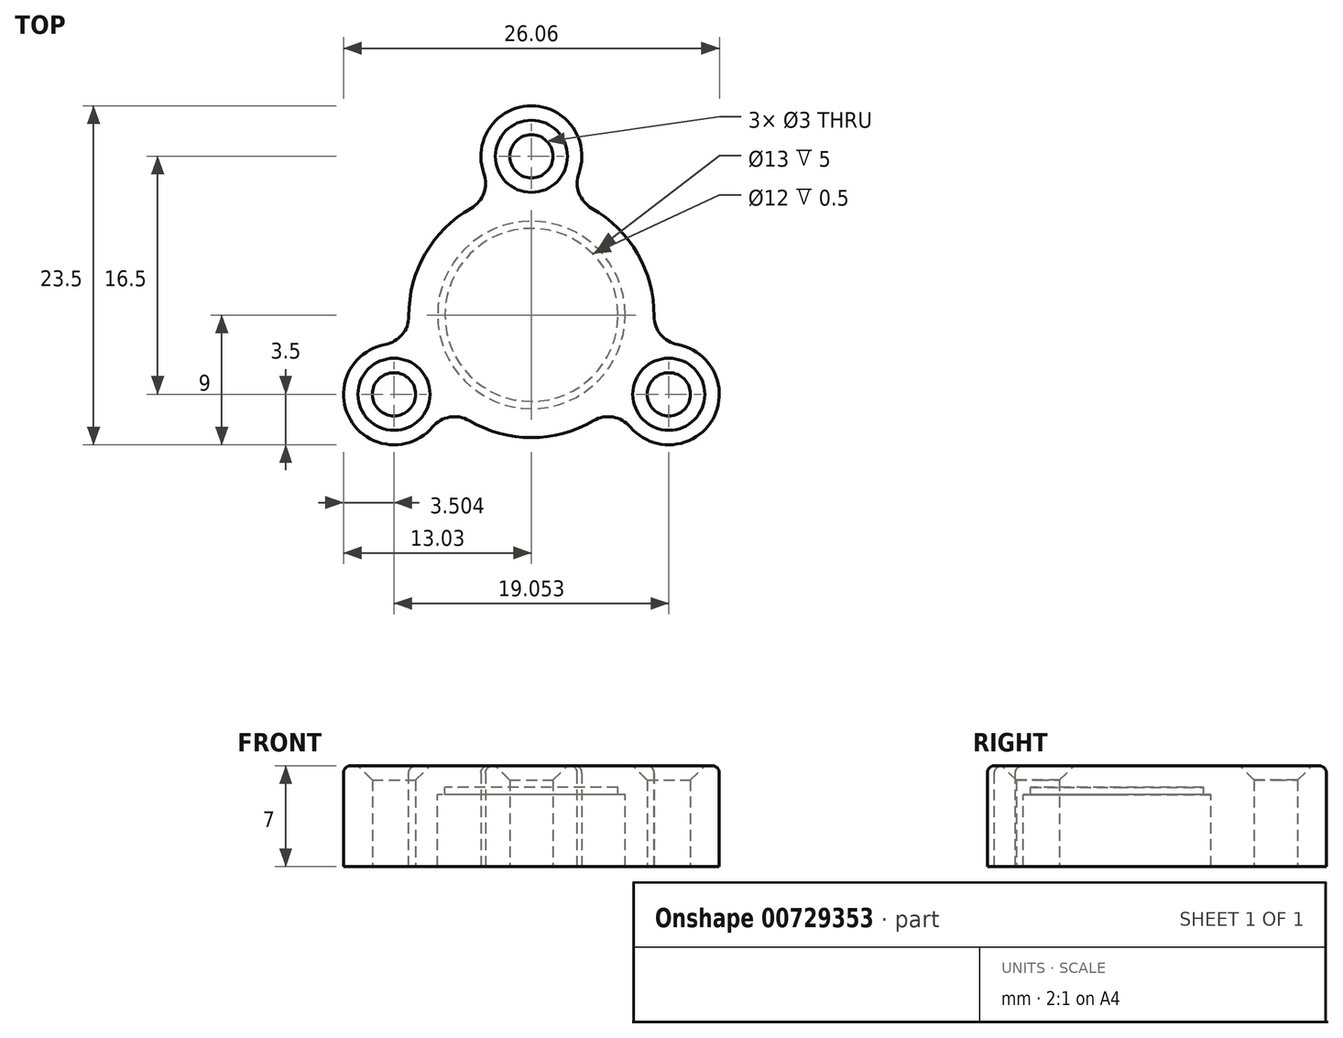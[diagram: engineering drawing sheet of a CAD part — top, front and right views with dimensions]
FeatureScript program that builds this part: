
annotation { "Feature Type Name" : "Feature", "Feature Type Description" : "" }
export const myFeature = defineFeature(function(context is Context, id is Id, definition is map)
    precondition{}
    {
        {
            var Q0;
            Q0=qCreatedBy(makeId("Right.planeOp"),FACE);
            var sketch = newSketch(context, id + "F0", { "sketchPlane" : qUnion([Q0])});
            skLineSegment(sketch, "E0", {"start": v(-8.5, 0) * mm, "end": v(-8.5, 7) * mm});
            skLineSegment(sketch, "E1", {"start": v(-8.5, 7) * mm, "end": v(0, 7) * mm});
            skLineSegment(sketch, "E2", {"start": v(0, 7) * mm, "end": v(0, 5.5) * mm});
            skLineSegment(sketch, "E3", {"start": v(-6, 5) * mm, "end": v(-6.5, 5) * mm});
            skLineSegment(sketch, "E4", {"start": v(-6.5, 5) * mm, "end": v(-6.5, 0) * mm});
            skLineSegment(sketch, "E5", {"start": v(-6.5, 0) * mm, "end": v(-8.5, 0) * mm});
            skLineSegment(sketch, "E6.top", {"start": v(-6, 5.5) * mm, "end": v(0, 5.5) * mm});
            skLineSegment(sketch, "E6.left", {"start": v(-6, 5) * mm, "end": v(-6, 5.5) * mm});
            skSolve(sketch);
        }
        {
            var Q0;
            Q0=makeQuery(id+"F0.imprint","IMPRINT",FACE,{"disambiguationData":[TD([[makeQuery(id+"F0.imprint","IMPRINT",EDGE,{"derivedFrom":sQuery(id+"F0.wireOp",EDGE,"E0")}),-1.0]])]});
            var Q1;
            Q1=sQuery(id+"F0.wireOp",EDGE,"E2");
            revolve(context, id + "F1", {"surfaceOperationType" : NewSurfaceOperationType.NEW, "entities" : qUnion([Q0]), "axis" : qUnion([Q1]), "revolveType" : RevolveType.FULL});
        }
        {
            var Q0;
            Q0=qCreatedBy(makeId("Top.planeOp"),FACE);
            var sketch = newSketch(context, id + "F2", { "sketchPlane" : qUnion([Q0])});
            skLineSegment(sketch, "E7", {"start": v(0, 11) * mm, "end": v(0, -13.89) * mm, "construction": true});
            skCircle(sketch, "E8", {"center": v(0, 11) * mm, "radius": 3.5 * mm});
            skCircle(sketch, "E9", {"center": v(0, 11) * mm, "radius": 1.5 * mm});
            skPoint(sketch, "E10", {"position": v(0, 0) * mm});
            skCircle(sketch, "E11.1.0", {"center": v(-9.53, -5.5) * mm, "radius": 3.5 * mm});
            skCircle(sketch, "E11.1.1", {"center": v(-9.53, -5.5) * mm, "radius": 1.5 * mm});
            skCircle(sketch, "E11.2.0", {"center": v(9.53, -5.5) * mm, "radius": 3.5 * mm});
            skCircle(sketch, "E11.2.1", {"center": v(9.53, -5.5) * mm, "radius": 1.5 * mm});
            skSolve(sketch);
        }
        {
            var Q0;
            Q0=makeQuery(id+"F2.imprint","IMPRINT",FACE,{"disambiguationData":[TD([[makeQuery(id+"F2.imprint","IMPRINT",EDGE,{"derivedFrom":sQuery(id+"F2.wireOp",EDGE,"E8")}),1.0]])]});
            var Q1;
            Q1=makeQuery(id+"F2.imprint","IMPRINT",FACE,{"disambiguationData":[TD([[makeQuery(id+"F2.imprint","IMPRINT",EDGE,{"derivedFrom":sQuery(id+"F2.wireOp",EDGE,"E11.1.0")}),1.0]])]});
            var Q2;
            Q2=makeQuery(id+"F2.imprint","IMPRINT",FACE,{"disambiguationData":[TD([[makeQuery(id+"F2.imprint","IMPRINT",EDGE,{"derivedFrom":sQuery(id+"F2.wireOp",EDGE,"E11.2.0")}),1.0]])]});
            extrude(context, id + "F3", {"entities" : qUnion([Q0, Q1, Q2]), "operationType" : NewBodyOperationType.ADD, "depth" : 7 * mm, "offsetDistance" : 25 * mm});
        }
        {
            var Q0;
            Q0=makeQuery(id+"F3.opExtrude","CAP_EDGE",EDGE,{"disambiguationData":[OSD([sQuery(id+"F2.wireOp",EDGE,"E9")])],"isStart":false});
            var Q1;
            Q1=makeQuery(id+"F3.opExtrude","CAP_EDGE",EDGE,{"disambiguationData":[OSD([sQuery(id+"F2.wireOp",EDGE,"E11.1.1")])],"isStart":false});
            var Q2;
            Q2=makeQuery(id+"F3.opExtrude","CAP_EDGE",EDGE,{"disambiguationData":[OSD([sQuery(id+"F2.wireOp",EDGE,"E11.2.1")])],"isStart":false});
            chamfer(context, id + "F4", {"entities" : qUnion([Q0, Q1, Q2]), "width" : 1 * mm, "tangentPropagation" : true});
        }
        {
            var Q0;
            Q0=makeQuery(id+"F3.boolean.opBoolean","INTERSECT",EDGE,{"disambiguationData":[OD(0.0)],"derivedFrom":[makeQuery(id+"F1.opRevolve","SWEPT_FACE",FACE,{"disambiguationData":[OSD([sQuery(id+"F0.wireOp",EDGE,"E0")])]}),makeQuery(id+"F3.opExtrude","SWEPT_FACE",FACE,{"disambiguationData":[OSD([sQuery(id+"F2.wireOp",EDGE,"E8")])]})]});
            var Q1;
            Q1=makeQuery(id+"F3.boolean.opBoolean","INTERSECT",EDGE,{"disambiguationData":[OD(0.0)],"derivedFrom":[makeQuery(id+"F1.opRevolve","SWEPT_FACE",FACE,{"disambiguationData":[OSD([sQuery(id+"F0.wireOp",EDGE,"E0")])]}),makeQuery(id+"F3.opExtrude","SWEPT_FACE",FACE,{"disambiguationData":[OSD([sQuery(id+"F2.wireOp",EDGE,"E11.1.0")])]})]});
            var Q2;
            Q2=makeQuery(id+"F3.boolean.opBoolean","INTERSECT",EDGE,{"disambiguationData":[OD(1.0)],"derivedFrom":[makeQuery(id+"F1.opRevolve","SWEPT_FACE",FACE,{"disambiguationData":[OSD([sQuery(id+"F0.wireOp",EDGE,"E0")])]}),makeQuery(id+"F3.opExtrude","SWEPT_FACE",FACE,{"disambiguationData":[OSD([sQuery(id+"F2.wireOp",EDGE,"E11.1.0")])]})]});
            var Q3;
            Q3=makeQuery(id+"F3.boolean.opBoolean","INTERSECT",EDGE,{"disambiguationData":[OD(1.0)],"derivedFrom":[makeQuery(id+"F1.opRevolve","SWEPT_FACE",FACE,{"disambiguationData":[OSD([sQuery(id+"F0.wireOp",EDGE,"E0")])]}),makeQuery(id+"F3.opExtrude","SWEPT_FACE",FACE,{"disambiguationData":[OSD([sQuery(id+"F2.wireOp",EDGE,"E11.2.0")])]})]});
            var Q4;
            Q4=makeQuery(id+"F3.boolean.opBoolean","INTERSECT",EDGE,{"disambiguationData":[OD(0.0)],"derivedFrom":[makeQuery(id+"F1.opRevolve","SWEPT_FACE",FACE,{"disambiguationData":[OSD([sQuery(id+"F0.wireOp",EDGE,"E0")])]}),makeQuery(id+"F3.opExtrude","SWEPT_FACE",FACE,{"disambiguationData":[OSD([sQuery(id+"F2.wireOp",EDGE,"E11.2.0")])]})]});
            var Q5;
            Q5=makeQuery(id+"F3.boolean.opBoolean","INTERSECT",EDGE,{"disambiguationData":[OD(1.0)],"derivedFrom":[makeQuery(id+"F1.opRevolve","SWEPT_FACE",FACE,{"disambiguationData":[OSD([sQuery(id+"F0.wireOp",EDGE,"E0")])]}),makeQuery(id+"F3.opExtrude","SWEPT_FACE",FACE,{"disambiguationData":[OSD([sQuery(id+"F2.wireOp",EDGE,"E8")])]})]});
            fillet(context, id + "F5", {"entities" : qUnion([Q0, Q1, Q2, Q3, Q4, Q5]), "radius" : 2 * mm, "tangentPropagation" : true, "allowEdgeOverflow" : false});
        }
        {
            var Q0;
            {var subQ0=sQuery(id+"F2.wireOp",EDGE,"E11.1.0");var subQ1=sQuery(id+"F0.wireOp",EDGE,"E1");var subQ2=sQuery(id+"F0.wireOp",EDGE,"E0");var subQ3=sQuery(id+"F2.wireOp",EDGE,"E11.2.0");Q0=makeQuery(id+"F3.boolean.opBoolean","SPLIT",EDGE,{"disambiguationData":[TD([makeQuery(id+"F1.opRevolve","SWEPT_FACE",FACE,{"disambiguationData":[OSD([subQ2])]}),makeQuery(id+"F1.opRevolve","SWEPT_FACE",FACE,{"disambiguationData":[OSD([subQ1])]}),makeQuery(id+"F3.opExtrude","CAP_FACE",FACE,{"disambiguationData":[OSD([sQuery(id+"F2.wireOp",EDGE,"E8"),sQuery(id+"F2.wireOp",EDGE,"E9")])],"isStart":false}),makeQuery(id+"F3.opExtrude","SWEPT_FACE",FACE,{"disambiguationData":[OSD([subQ0])]}),makeQuery(id+"F3.opExtrude","CAP_FACE",FACE,{"disambiguationData":[OSD([subQ0,sQuery(id+"F2.wireOp",EDGE,"E11.1.1")])],"isStart":false}),makeQuery(id+"F3.opExtrude","SWEPT_FACE",FACE,{"disambiguationData":[OSD([subQ3])]}),makeQuery(id+"F3.opExtrude","CAP_FACE",FACE,{"disambiguationData":[OSD([subQ3,sQuery(id+"F2.wireOp",EDGE,"E11.2.1")])],"isStart":false})])],"derivedFrom":makeQuery(id+"F1.opRevolve","SWEPT_EDGE",EDGE,{"disambiguationData":[OSD([subQ2,subQ1])]})});}
            var Q1;
            {var subQ0=sQuery(id+"F2.wireOp",EDGE,"E11.1.0");Q1=makeQuery(id+"F5.opFillet","BLEND_EDGE",EDGE,{"blendedFrom":[makeQuery(id+"F3.boolean.opBoolean","INTERSECT",EDGE,{"disambiguationData":[OD(1.0)],"derivedFrom":[makeQuery(id+"F1.opRevolve","SWEPT_FACE",FACE,{"disambiguationData":[OSD([sQuery(id+"F0.wireOp",EDGE,"E0")])]}),makeQuery(id+"F3.opExtrude","SWEPT_FACE",FACE,{"disambiguationData":[OSD([subQ0])]})]}),makeQuery(id+"F3.boolean.opBoolean","MERGE",FACE,{"derivedFrom":[makeQuery(id+"F1.opRevolve","SWEPT_FACE",FACE,{"disambiguationData":[OSD([sQuery(id+"F0.wireOp",EDGE,"E1")])]}),makeQuery(id+"F3.opExtrude","CAP_FACE",FACE,{"disambiguationData":[OSD([sQuery(id+"F2.wireOp",EDGE,"E8"),sQuery(id+"F2.wireOp",EDGE,"E9")])],"isStart":false}),makeQuery(id+"F3.opExtrude","CAP_FACE",FACE,{"disambiguationData":[OSD([subQ0,sQuery(id+"F2.wireOp",EDGE,"E11.1.1")])],"isStart":false}),makeQuery(id+"F3.opExtrude","CAP_FACE",FACE,{"disambiguationData":[OSD([sQuery(id+"F2.wireOp",EDGE,"E11.2.0"),sQuery(id+"F2.wireOp",EDGE,"E11.2.1")])],"isStart":false})]})],"blendedInto":[makeQuery(id+"F3.boolean.opBoolean","MERGE",FACE,{"derivedFrom":[makeQuery(id+"F1.opRevolve","SWEPT_FACE",FACE,{"disambiguationData":[OSD([sQuery(id+"F0.wireOp",EDGE,"E1")])]}),makeQuery(id+"F3.opExtrude","CAP_FACE",FACE,{"disambiguationData":[OSD([sQuery(id+"F2.wireOp",EDGE,"E8"),sQuery(id+"F2.wireOp",EDGE,"E9")])],"isStart":false}),makeQuery(id+"F3.opExtrude","CAP_FACE",FACE,{"disambiguationData":[OSD([subQ0,sQuery(id+"F2.wireOp",EDGE,"E11.1.1")])],"isStart":false}),makeQuery(id+"F3.opExtrude","CAP_FACE",FACE,{"disambiguationData":[OSD([sQuery(id+"F2.wireOp",EDGE,"E11.2.0"),sQuery(id+"F2.wireOp",EDGE,"E11.2.1")])],"isStart":false})]})]});}
            var Q2;
            Q2=makeQuery(id+"F3.opExtrude","CAP_EDGE",EDGE,{"disambiguationData":[OSD([sQuery(id+"F2.wireOp",EDGE,"E11.1.0")])],"isStart":false});
            var Q3;
            {var subQ0=sQuery(id+"F2.wireOp",EDGE,"E11.1.0");Q3=makeQuery(id+"F5.opFillet","BLEND_EDGE",EDGE,{"blendedFrom":[makeQuery(id+"F3.boolean.opBoolean","INTERSECT",EDGE,{"disambiguationData":[OD(0.0)],"derivedFrom":[makeQuery(id+"F1.opRevolve","SWEPT_FACE",FACE,{"disambiguationData":[OSD([sQuery(id+"F0.wireOp",EDGE,"E0")])]}),makeQuery(id+"F3.opExtrude","SWEPT_FACE",FACE,{"disambiguationData":[OSD([subQ0])]})]}),makeQuery(id+"F3.boolean.opBoolean","MERGE",FACE,{"derivedFrom":[makeQuery(id+"F1.opRevolve","SWEPT_FACE",FACE,{"disambiguationData":[OSD([sQuery(id+"F0.wireOp",EDGE,"E1")])]}),makeQuery(id+"F3.opExtrude","CAP_FACE",FACE,{"disambiguationData":[OSD([sQuery(id+"F2.wireOp",EDGE,"E8"),sQuery(id+"F2.wireOp",EDGE,"E9")])],"isStart":false}),makeQuery(id+"F3.opExtrude","CAP_FACE",FACE,{"disambiguationData":[OSD([subQ0,sQuery(id+"F2.wireOp",EDGE,"E11.1.1")])],"isStart":false}),makeQuery(id+"F3.opExtrude","CAP_FACE",FACE,{"disambiguationData":[OSD([sQuery(id+"F2.wireOp",EDGE,"E11.2.0"),sQuery(id+"F2.wireOp",EDGE,"E11.2.1")])],"isStart":false})]})],"blendedInto":[makeQuery(id+"F3.boolean.opBoolean","MERGE",FACE,{"derivedFrom":[makeQuery(id+"F1.opRevolve","SWEPT_FACE",FACE,{"disambiguationData":[OSD([sQuery(id+"F0.wireOp",EDGE,"E1")])]}),makeQuery(id+"F3.opExtrude","CAP_FACE",FACE,{"disambiguationData":[OSD([sQuery(id+"F2.wireOp",EDGE,"E8"),sQuery(id+"F2.wireOp",EDGE,"E9")])],"isStart":false}),makeQuery(id+"F3.opExtrude","CAP_FACE",FACE,{"disambiguationData":[OSD([subQ0,sQuery(id+"F2.wireOp",EDGE,"E11.1.1")])],"isStart":false}),makeQuery(id+"F3.opExtrude","CAP_FACE",FACE,{"disambiguationData":[OSD([sQuery(id+"F2.wireOp",EDGE,"E11.2.0"),sQuery(id+"F2.wireOp",EDGE,"E11.2.1")])],"isStart":false})]})]});}
            var Q4;
            {var subQ0=sQuery(id+"F2.wireOp",EDGE,"E8");var subQ1=sQuery(id+"F0.wireOp",EDGE,"E1");var subQ2=sQuery(id+"F0.wireOp",EDGE,"E0");var subQ3=sQuery(id+"F2.wireOp",EDGE,"E11.1.0");Q4=makeQuery(id+"F3.boolean.opBoolean","SPLIT",EDGE,{"disambiguationData":[TD([makeQuery(id+"F1.opRevolve","SWEPT_FACE",FACE,{"disambiguationData":[OSD([subQ2])]}),makeQuery(id+"F1.opRevolve","SWEPT_FACE",FACE,{"disambiguationData":[OSD([subQ1])]}),makeQuery(id+"F3.opExtrude","SWEPT_FACE",FACE,{"disambiguationData":[OSD([subQ0])]}),makeQuery(id+"F3.opExtrude","CAP_FACE",FACE,{"disambiguationData":[OSD([subQ0,sQuery(id+"F2.wireOp",EDGE,"E9")])],"isStart":false}),makeQuery(id+"F3.opExtrude","SWEPT_FACE",FACE,{"disambiguationData":[OSD([subQ3])]}),makeQuery(id+"F3.opExtrude","CAP_FACE",FACE,{"disambiguationData":[OSD([subQ3,sQuery(id+"F2.wireOp",EDGE,"E11.1.1")])],"isStart":false}),makeQuery(id+"F3.opExtrude","CAP_FACE",FACE,{"disambiguationData":[OSD([sQuery(id+"F2.wireOp",EDGE,"E11.2.0"),sQuery(id+"F2.wireOp",EDGE,"E11.2.1")])],"isStart":false})])],"derivedFrom":makeQuery(id+"F1.opRevolve","SWEPT_EDGE",EDGE,{"disambiguationData":[OSD([subQ2,subQ1])]})});}
            var Q5;
            {var subQ0=sQuery(id+"F2.wireOp",EDGE,"E8");Q5=makeQuery(id+"F5.opFillet","BLEND_EDGE",EDGE,{"blendedFrom":[makeQuery(id+"F3.boolean.opBoolean","INTERSECT",EDGE,{"disambiguationData":[OD(0.0)],"derivedFrom":[makeQuery(id+"F1.opRevolve","SWEPT_FACE",FACE,{"disambiguationData":[OSD([sQuery(id+"F0.wireOp",EDGE,"E0")])]}),makeQuery(id+"F3.opExtrude","SWEPT_FACE",FACE,{"disambiguationData":[OSD([subQ0])]})]}),makeQuery(id+"F3.boolean.opBoolean","MERGE",FACE,{"derivedFrom":[makeQuery(id+"F1.opRevolve","SWEPT_FACE",FACE,{"disambiguationData":[OSD([sQuery(id+"F0.wireOp",EDGE,"E1")])]}),makeQuery(id+"F3.opExtrude","CAP_FACE",FACE,{"disambiguationData":[OSD([subQ0,sQuery(id+"F2.wireOp",EDGE,"E9")])],"isStart":false}),makeQuery(id+"F3.opExtrude","CAP_FACE",FACE,{"disambiguationData":[OSD([sQuery(id+"F2.wireOp",EDGE,"E11.1.0"),sQuery(id+"F2.wireOp",EDGE,"E11.1.1")])],"isStart":false}),makeQuery(id+"F3.opExtrude","CAP_FACE",FACE,{"disambiguationData":[OSD([sQuery(id+"F2.wireOp",EDGE,"E11.2.0"),sQuery(id+"F2.wireOp",EDGE,"E11.2.1")])],"isStart":false})]})],"blendedInto":[makeQuery(id+"F3.boolean.opBoolean","MERGE",FACE,{"derivedFrom":[makeQuery(id+"F1.opRevolve","SWEPT_FACE",FACE,{"disambiguationData":[OSD([sQuery(id+"F0.wireOp",EDGE,"E1")])]}),makeQuery(id+"F3.opExtrude","CAP_FACE",FACE,{"disambiguationData":[OSD([subQ0,sQuery(id+"F2.wireOp",EDGE,"E9")])],"isStart":false}),makeQuery(id+"F3.opExtrude","CAP_FACE",FACE,{"disambiguationData":[OSD([sQuery(id+"F2.wireOp",EDGE,"E11.1.0"),sQuery(id+"F2.wireOp",EDGE,"E11.1.1")])],"isStart":false}),makeQuery(id+"F3.opExtrude","CAP_FACE",FACE,{"disambiguationData":[OSD([sQuery(id+"F2.wireOp",EDGE,"E11.2.0"),sQuery(id+"F2.wireOp",EDGE,"E11.2.1")])],"isStart":false})]})]});}
            var Q6;
            Q6=makeQuery(id+"F3.opExtrude","CAP_EDGE",EDGE,{"disambiguationData":[OSD([sQuery(id+"F2.wireOp",EDGE,"E8")])],"isStart":false});
            var Q7;
            {var subQ0=sQuery(id+"F2.wireOp",EDGE,"E8");var subQ1=sQuery(id+"F0.wireOp",EDGE,"E1");var subQ2=sQuery(id+"F0.wireOp",EDGE,"E0");var subQ3=sQuery(id+"F2.wireOp",EDGE,"E11.2.0");Q7=makeQuery(id+"F3.boolean.opBoolean","SPLIT",EDGE,{"disambiguationData":[TD([makeQuery(id+"F1.opRevolve","SWEPT_FACE",FACE,{"disambiguationData":[OSD([subQ2])]}),makeQuery(id+"F1.opRevolve","SWEPT_FACE",FACE,{"disambiguationData":[OSD([subQ1])]}),makeQuery(id+"F3.opExtrude","SWEPT_FACE",FACE,{"disambiguationData":[OSD([subQ0])]}),makeQuery(id+"F3.opExtrude","CAP_FACE",FACE,{"disambiguationData":[OSD([subQ0,sQuery(id+"F2.wireOp",EDGE,"E9")])],"isStart":false}),makeQuery(id+"F3.opExtrude","CAP_FACE",FACE,{"disambiguationData":[OSD([sQuery(id+"F2.wireOp",EDGE,"E11.1.0"),sQuery(id+"F2.wireOp",EDGE,"E11.1.1")])],"isStart":false}),makeQuery(id+"F3.opExtrude","SWEPT_FACE",FACE,{"disambiguationData":[OSD([subQ3])]}),makeQuery(id+"F3.opExtrude","CAP_FACE",FACE,{"disambiguationData":[OSD([subQ3,sQuery(id+"F2.wireOp",EDGE,"E11.2.1")])],"isStart":false})])],"derivedFrom":makeQuery(id+"F1.opRevolve","SWEPT_EDGE",EDGE,{"disambiguationData":[OSD([subQ2,subQ1])]})});}
            var Q8;
            {var subQ0=sQuery(id+"F2.wireOp",EDGE,"E8");Q8=makeQuery(id+"F5.opFillet","BLEND_EDGE",EDGE,{"blendedFrom":[makeQuery(id+"F3.boolean.opBoolean","INTERSECT",EDGE,{"disambiguationData":[OD(1.0)],"derivedFrom":[makeQuery(id+"F1.opRevolve","SWEPT_FACE",FACE,{"disambiguationData":[OSD([sQuery(id+"F0.wireOp",EDGE,"E0")])]}),makeQuery(id+"F3.opExtrude","SWEPT_FACE",FACE,{"disambiguationData":[OSD([subQ0])]})]}),makeQuery(id+"F3.boolean.opBoolean","MERGE",FACE,{"derivedFrom":[makeQuery(id+"F1.opRevolve","SWEPT_FACE",FACE,{"disambiguationData":[OSD([sQuery(id+"F0.wireOp",EDGE,"E1")])]}),makeQuery(id+"F3.opExtrude","CAP_FACE",FACE,{"disambiguationData":[OSD([subQ0,sQuery(id+"F2.wireOp",EDGE,"E9")])],"isStart":false}),makeQuery(id+"F3.opExtrude","CAP_FACE",FACE,{"disambiguationData":[OSD([sQuery(id+"F2.wireOp",EDGE,"E11.1.0"),sQuery(id+"F2.wireOp",EDGE,"E11.1.1")])],"isStart":false}),makeQuery(id+"F3.opExtrude","CAP_FACE",FACE,{"disambiguationData":[OSD([sQuery(id+"F2.wireOp",EDGE,"E11.2.0"),sQuery(id+"F2.wireOp",EDGE,"E11.2.1")])],"isStart":false})]})],"blendedInto":[makeQuery(id+"F3.boolean.opBoolean","MERGE",FACE,{"derivedFrom":[makeQuery(id+"F1.opRevolve","SWEPT_FACE",FACE,{"disambiguationData":[OSD([sQuery(id+"F0.wireOp",EDGE,"E1")])]}),makeQuery(id+"F3.opExtrude","CAP_FACE",FACE,{"disambiguationData":[OSD([subQ0,sQuery(id+"F2.wireOp",EDGE,"E9")])],"isStart":false}),makeQuery(id+"F3.opExtrude","CAP_FACE",FACE,{"disambiguationData":[OSD([sQuery(id+"F2.wireOp",EDGE,"E11.1.0"),sQuery(id+"F2.wireOp",EDGE,"E11.1.1")])],"isStart":false}),makeQuery(id+"F3.opExtrude","CAP_FACE",FACE,{"disambiguationData":[OSD([sQuery(id+"F2.wireOp",EDGE,"E11.2.0"),sQuery(id+"F2.wireOp",EDGE,"E11.2.1")])],"isStart":false})]})]});}
            var Q9;
            {var subQ0=sQuery(id+"F2.wireOp",EDGE,"E11.2.0");Q9=makeQuery(id+"F5.opFillet","BLEND_EDGE",EDGE,{"blendedFrom":[makeQuery(id+"F3.boolean.opBoolean","INTERSECT",EDGE,{"disambiguationData":[OD(0.0)],"derivedFrom":[makeQuery(id+"F1.opRevolve","SWEPT_FACE",FACE,{"disambiguationData":[OSD([sQuery(id+"F0.wireOp",EDGE,"E0")])]}),makeQuery(id+"F3.opExtrude","SWEPT_FACE",FACE,{"disambiguationData":[OSD([subQ0])]})]}),makeQuery(id+"F3.boolean.opBoolean","MERGE",FACE,{"derivedFrom":[makeQuery(id+"F1.opRevolve","SWEPT_FACE",FACE,{"disambiguationData":[OSD([sQuery(id+"F0.wireOp",EDGE,"E1")])]}),makeQuery(id+"F3.opExtrude","CAP_FACE",FACE,{"disambiguationData":[OSD([sQuery(id+"F2.wireOp",EDGE,"E8"),sQuery(id+"F2.wireOp",EDGE,"E9")])],"isStart":false}),makeQuery(id+"F3.opExtrude","CAP_FACE",FACE,{"disambiguationData":[OSD([sQuery(id+"F2.wireOp",EDGE,"E11.1.0"),sQuery(id+"F2.wireOp",EDGE,"E11.1.1")])],"isStart":false}),makeQuery(id+"F3.opExtrude","CAP_FACE",FACE,{"disambiguationData":[OSD([subQ0,sQuery(id+"F2.wireOp",EDGE,"E11.2.1")])],"isStart":false})]})],"blendedInto":[makeQuery(id+"F3.boolean.opBoolean","MERGE",FACE,{"derivedFrom":[makeQuery(id+"F1.opRevolve","SWEPT_FACE",FACE,{"disambiguationData":[OSD([sQuery(id+"F0.wireOp",EDGE,"E1")])]}),makeQuery(id+"F3.opExtrude","CAP_FACE",FACE,{"disambiguationData":[OSD([sQuery(id+"F2.wireOp",EDGE,"E8"),sQuery(id+"F2.wireOp",EDGE,"E9")])],"isStart":false}),makeQuery(id+"F3.opExtrude","CAP_FACE",FACE,{"disambiguationData":[OSD([sQuery(id+"F2.wireOp",EDGE,"E11.1.0"),sQuery(id+"F2.wireOp",EDGE,"E11.1.1")])],"isStart":false}),makeQuery(id+"F3.opExtrude","CAP_FACE",FACE,{"disambiguationData":[OSD([subQ0,sQuery(id+"F2.wireOp",EDGE,"E11.2.1")])],"isStart":false})]})]});}
            var Q10;
            Q10=makeQuery(id+"F3.opExtrude","CAP_EDGE",EDGE,{"disambiguationData":[OSD([sQuery(id+"F2.wireOp",EDGE,"E11.2.0")])],"isStart":false});
            var Q11;
            {var subQ0=sQuery(id+"F2.wireOp",EDGE,"E11.2.0");Q11=makeQuery(id+"F5.opFillet","BLEND_EDGE",EDGE,{"blendedFrom":[makeQuery(id+"F3.boolean.opBoolean","INTERSECT",EDGE,{"disambiguationData":[OD(1.0)],"derivedFrom":[makeQuery(id+"F1.opRevolve","SWEPT_FACE",FACE,{"disambiguationData":[OSD([sQuery(id+"F0.wireOp",EDGE,"E0")])]}),makeQuery(id+"F3.opExtrude","SWEPT_FACE",FACE,{"disambiguationData":[OSD([subQ0])]})]}),makeQuery(id+"F3.boolean.opBoolean","MERGE",FACE,{"derivedFrom":[makeQuery(id+"F1.opRevolve","SWEPT_FACE",FACE,{"disambiguationData":[OSD([sQuery(id+"F0.wireOp",EDGE,"E1")])]}),makeQuery(id+"F3.opExtrude","CAP_FACE",FACE,{"disambiguationData":[OSD([sQuery(id+"F2.wireOp",EDGE,"E8"),sQuery(id+"F2.wireOp",EDGE,"E9")])],"isStart":false}),makeQuery(id+"F3.opExtrude","CAP_FACE",FACE,{"disambiguationData":[OSD([sQuery(id+"F2.wireOp",EDGE,"E11.1.0"),sQuery(id+"F2.wireOp",EDGE,"E11.1.1")])],"isStart":false}),makeQuery(id+"F3.opExtrude","CAP_FACE",FACE,{"disambiguationData":[OSD([subQ0,sQuery(id+"F2.wireOp",EDGE,"E11.2.1")])],"isStart":false})]})],"blendedInto":[makeQuery(id+"F3.boolean.opBoolean","MERGE",FACE,{"derivedFrom":[makeQuery(id+"F1.opRevolve","SWEPT_FACE",FACE,{"disambiguationData":[OSD([sQuery(id+"F0.wireOp",EDGE,"E1")])]}),makeQuery(id+"F3.opExtrude","CAP_FACE",FACE,{"disambiguationData":[OSD([sQuery(id+"F2.wireOp",EDGE,"E8"),sQuery(id+"F2.wireOp",EDGE,"E9")])],"isStart":false}),makeQuery(id+"F3.opExtrude","CAP_FACE",FACE,{"disambiguationData":[OSD([sQuery(id+"F2.wireOp",EDGE,"E11.1.0"),sQuery(id+"F2.wireOp",EDGE,"E11.1.1")])],"isStart":false}),makeQuery(id+"F3.opExtrude","CAP_FACE",FACE,{"disambiguationData":[OSD([subQ0,sQuery(id+"F2.wireOp",EDGE,"E11.2.1")])],"isStart":false})]})]});}
            fillet(context, id + "F6", {"entities" : qUnion([Q0, Q1, Q2, Q3, Q4, Q5, Q6, Q7, Q8, Q9, Q10, Q11]), "radius" : 0.5 * mm, "tangentPropagation" : true, "allowEdgeOverflow" : false});
        }
    });
